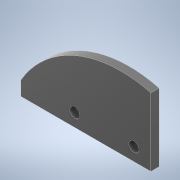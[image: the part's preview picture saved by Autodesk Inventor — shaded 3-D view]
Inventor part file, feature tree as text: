
AUTODESK INVENTOR PART (.ipt)
format: ipt  version: 2022 (Build 260153000, 153)  size: 116,224 bytes
history: native  units: mm
features: other x1, extrude x1, sketch x1
ambient origin geometry x8: Origin, YZ Plane, XZ Plane, XY Plane, X Axis, Y Axis, Z Axis, Center Point
bodies: Body1 (feature_tree)
feature tree (3):
  other  "FS90-Mount2.ipt"
  extrude  "押し出し1"  Depth=10.0mm
  sketch  "スケッチ1"
